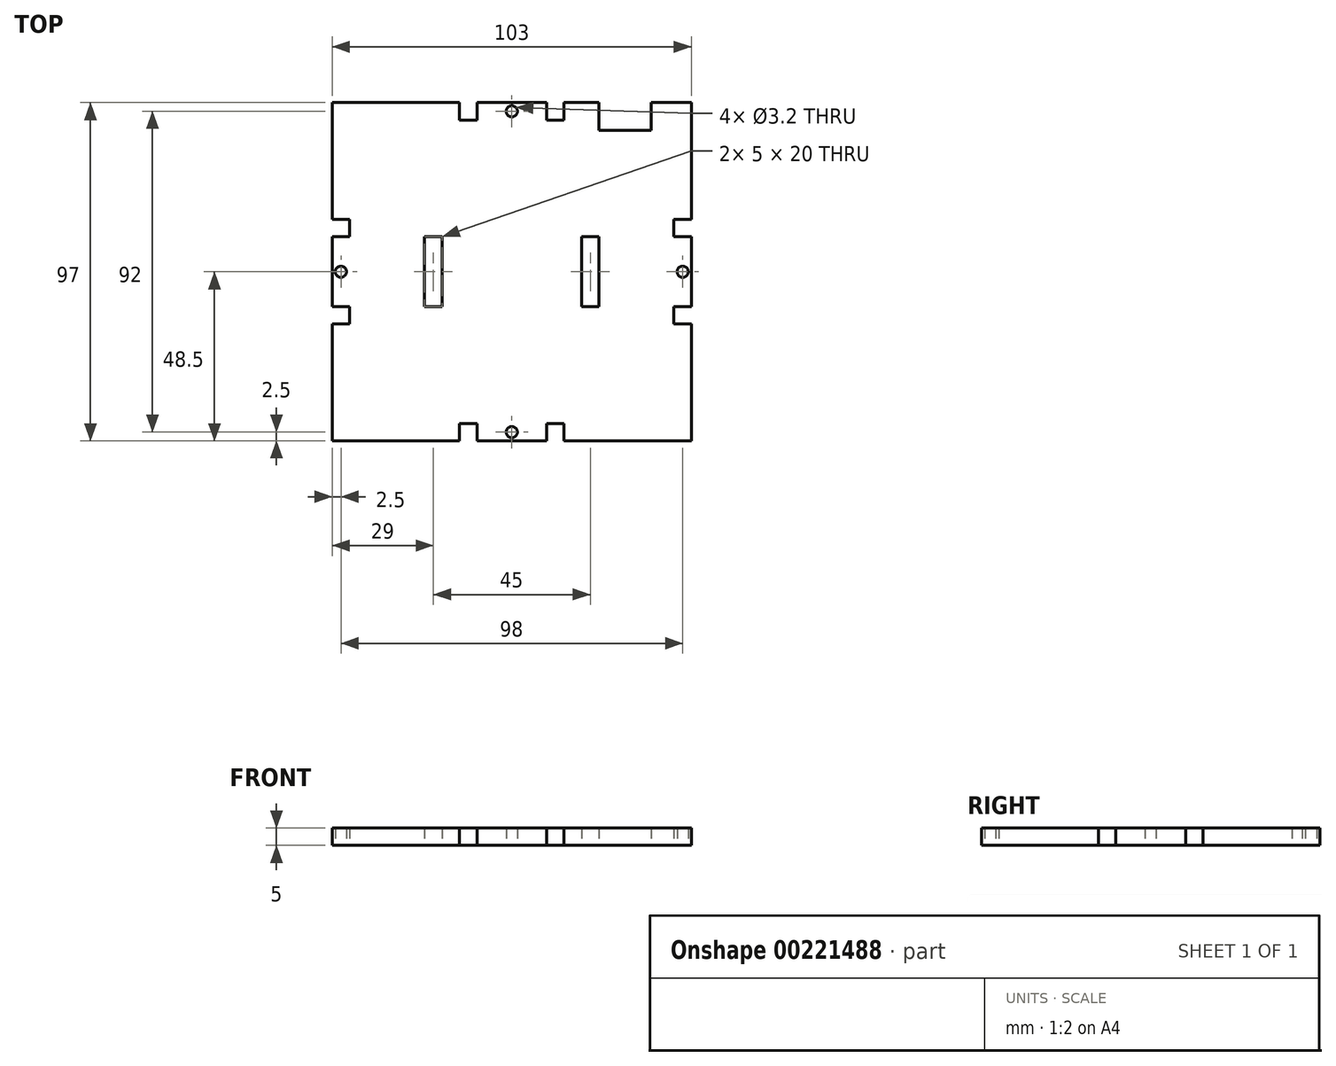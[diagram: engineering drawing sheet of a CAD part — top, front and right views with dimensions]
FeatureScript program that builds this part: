
annotation { "Feature Type Name" : "Feature", "Feature Type Description" : "" }
export const myFeature = defineFeature(function(context is Context, id is Id, definition is map)
    precondition{}
    {
        {
            assignVariable(context, id + "F0", {"name" : "thickness", "anyValue" : 5 * mm});
        }
        {
            var Q0;
            Q0=qCreatedBy(makeId("Top.planeOp"),FACE);
            var sketch = newSketch(context, id + "F1", { "sketchPlane" : qUnion([Q0])});
            skLineSegment(sketch, "E0.MirrorCS", {"start": v(41.5, 92) * mm, "end": v(41.5, 97) * mm});
            skPoint(sketch, "E1.MirrorP", {"position": v(41.5, 94.5) * mm});
            skLineSegment(sketch, "E2.MirrorCS", {"start": v(61.5, 92) * mm, "end": v(66.5, 92) * mm});
            skLineSegment(sketch, "E3.MirrorCS", {"start": v(36.5, 97) * mm, "end": v(36.5, 92) * mm});
            skLineSegment(sketch, "E4.MirrorCS", {"start": v(36.5, 92) * mm, "end": v(41.5, 92) * mm});
            skCircle(sketch, "E5.MirrorC", {"center": v(51.5, 94.5) * mm, "radius": 1.6 * mm});
            skLineSegment(sketch, "E6.MirrorCS", {"start": v(61.5, 97) * mm, "end": v(61.5, 92) * mm});
            skLineSegment(sketch, "E7.MirrorCS", {"start": v(66.5, 92) * mm, "end": v(66.5, 97) * mm});
            skLineSegment(sketch, "E8.MirrorCS", {"start": v(41.5, 97) * mm, "end": v(61.5, 97) * mm});
            skLineSegment(sketch, "E9.bottom", {"start": v(0, 0) * mm, "end": v(36.5, 0) * mm});
            skLineSegment(sketch, "E9.top", {"start": v(0, 97) * mm, "end": v(36.5, 97) * mm});
            skLineSegment(sketch, "E9.left", {"start": v(0, 0) * mm, "end": v(0, 33.5) * mm});
            skLineSegment(sketch, "E9.right", {"start": v(103, 0) * mm, "end": v(103, 33.5) * mm});
            skLineSegment(sketch, "E10", {"start": v(51.5, 0) * mm, "end": v(51.5, 97) * mm, "construction": true});
            skLineSegment(sketch, "E11", {"start": v(0, 48.5) * mm, "end": v(103, 48.5) * mm, "construction": true});
            skLineSegment(sketch, "E12.MirrorCS", {"start": v(41.5, 5) * mm, "end": v(41.5, 0) * mm});
            skLineSegment(sketch, "E13.MirrorCS", {"start": v(41.5, 0) * mm, "end": v(61.5, 0) * mm});
            skLineSegment(sketch, "E14.MirrorCS", {"start": v(61.5, 0) * mm, "end": v(61.5, 5) * mm});
            skLineSegment(sketch, "E15.MirrorCS", {"start": v(66.5, 5) * mm, "end": v(66.5, 0) * mm});
            skPoint(sketch, "E16.MirrorP", {"position": v(41.5, 2.5) * mm});
            skCircle(sketch, "E17.MirrorC", {"center": v(51.5, 2.5) * mm, "radius": 1.6 * mm});
            skLineSegment(sketch, "E18.MirrorCS", {"start": v(61.5, 5) * mm, "end": v(66.5, 5) * mm});
            skLineSegment(sketch, "E19.MirrorCS", {"start": v(36.5, 5) * mm, "end": v(41.5, 5) * mm});
            skLineSegment(sketch, "E20.MirrorCS", {"start": v(36.5, 0) * mm, "end": v(36.5, 5) * mm});
            skLineSegment(sketch, "E21.MirrorCS", {"start": v(5, 38.5) * mm, "end": v(0, 38.5) * mm});
            skPoint(sketch, "E22.MirrorP", {"position": v(2.5, 38.5) * mm});
            skLineSegment(sketch, "E23.MirrorCS", {"start": v(5, 58.5) * mm, "end": v(5, 63.5) * mm});
            skLineSegment(sketch, "E24.MirrorCS", {"start": v(0, 33.5) * mm, "end": v(5, 33.5) * mm});
            skLineSegment(sketch, "E25.MirrorCS", {"start": v(5, 33.5) * mm, "end": v(5, 38.5) * mm});
            skCircle(sketch, "E26.MirrorC", {"center": v(2.5, 48.5) * mm, "radius": 1.6 * mm});
            skLineSegment(sketch, "E27.MirrorCS", {"start": v(0, 58.5) * mm, "end": v(5, 58.5) * mm});
            skLineSegment(sketch, "E28.MirrorCS", {"start": v(5, 63.5) * mm, "end": v(0, 63.5) * mm});
            skLineSegment(sketch, "E29.MirrorCS", {"start": v(0, 38.5) * mm, "end": v(0, 58.5) * mm});
            skLineSegment(sketch, "E30.MirrorCS", {"start": v(98, 38.5) * mm, "end": v(103, 38.5) * mm});
            skPoint(sketch, "E31.MirrorP", {"position": v(100.5, 38.5) * mm});
            skCircle(sketch, "E32.MirrorC", {"center": v(100.5, 48.5) * mm, "radius": 1.6 * mm});
            skLineSegment(sketch, "E33.MirrorCS", {"start": v(98, 63.5) * mm, "end": v(103, 63.5) * mm});
            skLineSegment(sketch, "E34.MirrorCS", {"start": v(103, 33.5) * mm, "end": v(98, 33.5) * mm});
            skLineSegment(sketch, "E35.MirrorCS", {"start": v(98, 58.5) * mm, "end": v(98, 63.5) * mm});
            skLineSegment(sketch, "E36.MirrorCS", {"start": v(103, 38.5) * mm, "end": v(103, 58.5) * mm});
            skLineSegment(sketch, "E37.MirrorCS", {"start": v(98, 33.5) * mm, "end": v(98, 38.5) * mm});
            skLineSegment(sketch, "E38.MirrorCS", {"start": v(103, 58.5) * mm, "end": v(98, 58.5) * mm});
            skLineSegment(sketch, "E39.trimOffspring", {"start": v(66.5, 97) * mm, "end": v(76.5, 97) * mm});
            skLineSegment(sketch, "E40.trimOffspring", {"start": v(0, 63.5) * mm, "end": v(0, 97) * mm});
            skLineSegment(sketch, "E41.trimOffspring", {"start": v(103, 63.5) * mm, "end": v(103, 97) * mm});
            skLineSegment(sketch, "E42.trimOffspring", {"start": v(66.5, 0) * mm, "end": v(103, 0) * mm});
            skLineSegment(sketch, "E43", {"start": v(76.5, 97) * mm, "end": v(76.5, 89) * mm});
            skLineSegment(sketch, "E44", {"start": v(76.5, 89) * mm, "end": v(91.5, 89) * mm});
            skLineSegment(sketch, "E45", {"start": v(91.5, 89) * mm, "end": v(91.5, 97) * mm});
            skLineSegment(sketch, "E46.trimOffspring", {"start": v(91.5, 97) * mm, "end": v(103, 97) * mm});
            skLineSegment(sketch, "E47.bottom", {"start": v(26.5, 58.5) * mm, "end": v(31.5, 58.5) * mm});
            skLineSegment(sketch, "E47.top", {"start": v(26.5, 38.5) * mm, "end": v(31.5, 38.5) * mm});
            skLineSegment(sketch, "E47.left", {"start": v(26.5, 58.5) * mm, "end": v(26.5, 38.5) * mm});
            skLineSegment(sketch, "E47.right", {"start": v(31.5, 58.5) * mm, "end": v(31.5, 38.5) * mm});
            skPoint(sketch, "E48", {"position": v(31.5, 48.5) * mm});
            skPoint(sketch, "E49.MirrorP", {"position": v(71.5, 48.5) * mm});
            skLineSegment(sketch, "E50.MirrorCS", {"start": v(71.5, 58.5) * mm, "end": v(71.5, 38.5) * mm});
            skLineSegment(sketch, "E51.MirrorCS", {"start": v(76.5, 58.5) * mm, "end": v(76.5, 38.5) * mm});
            skLineSegment(sketch, "E52.MirrorCS", {"start": v(76.5, 58.5) * mm, "end": v(71.5, 58.5) * mm});
            skLineSegment(sketch, "E53.MirrorCS", {"start": v(76.5, 38.5) * mm, "end": v(71.5, 38.5) * mm});
            skSolve(sketch);
        }
        {
            var Q0;
            Q0 = qSketchRegion(id + "F1", true);
            extrude(context, id + "F2", {"entities" : qUnion([Q0]), "depth" : getVariable(context, 'thickness')});
        }
    });
